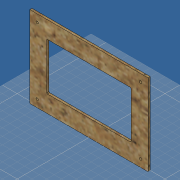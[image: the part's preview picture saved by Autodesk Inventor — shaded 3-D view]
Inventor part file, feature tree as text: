
AUTODESK INVENTOR PART (.ipt)
format: ipt  version: 2019 (Build 230136000, 136)  size: 152,064 bytes
history: native  units: mm
features: extrude x2, other x1, sketch x1
ambient origin geometry x8: Origin, YZ Plane, XZ Plane, XY Plane, X Axis, Y Axis, Z Axis, Center Point
bodies: Volumenkörper1 (feature_tree)
feature tree (4):
  other  "<userpath>\OneDrive\Dokumente\Inventor\Absauganlage\Absauganlage_Params.xlsx"
  sketch  "Skizze1"  dims[d0=140.0mm d1=240.0mm d2=5.0mm d3=232.0mm d4=132.0mm d5=2.0mm d6=128.0mm d7=228.0mm d8=2.0mm d9=40.0mm d10=40.0mm d11=6.5mm d12=20.0mm d13=20.0mm d14=6.0mm d15=0.0mm d16=6.0mm d17=0.0mm]
  extrude  "Extrusion1"  Depth=6.0mm
  extrude  "Extrusion2"  TaperAngle=0.0deg  [1 undecoded]
note: 1 required parameter value undecoded (feature->parameter linkage not recoverable at this tier; creation-order binding heuristic only, values carry confidence <= 0.55)
